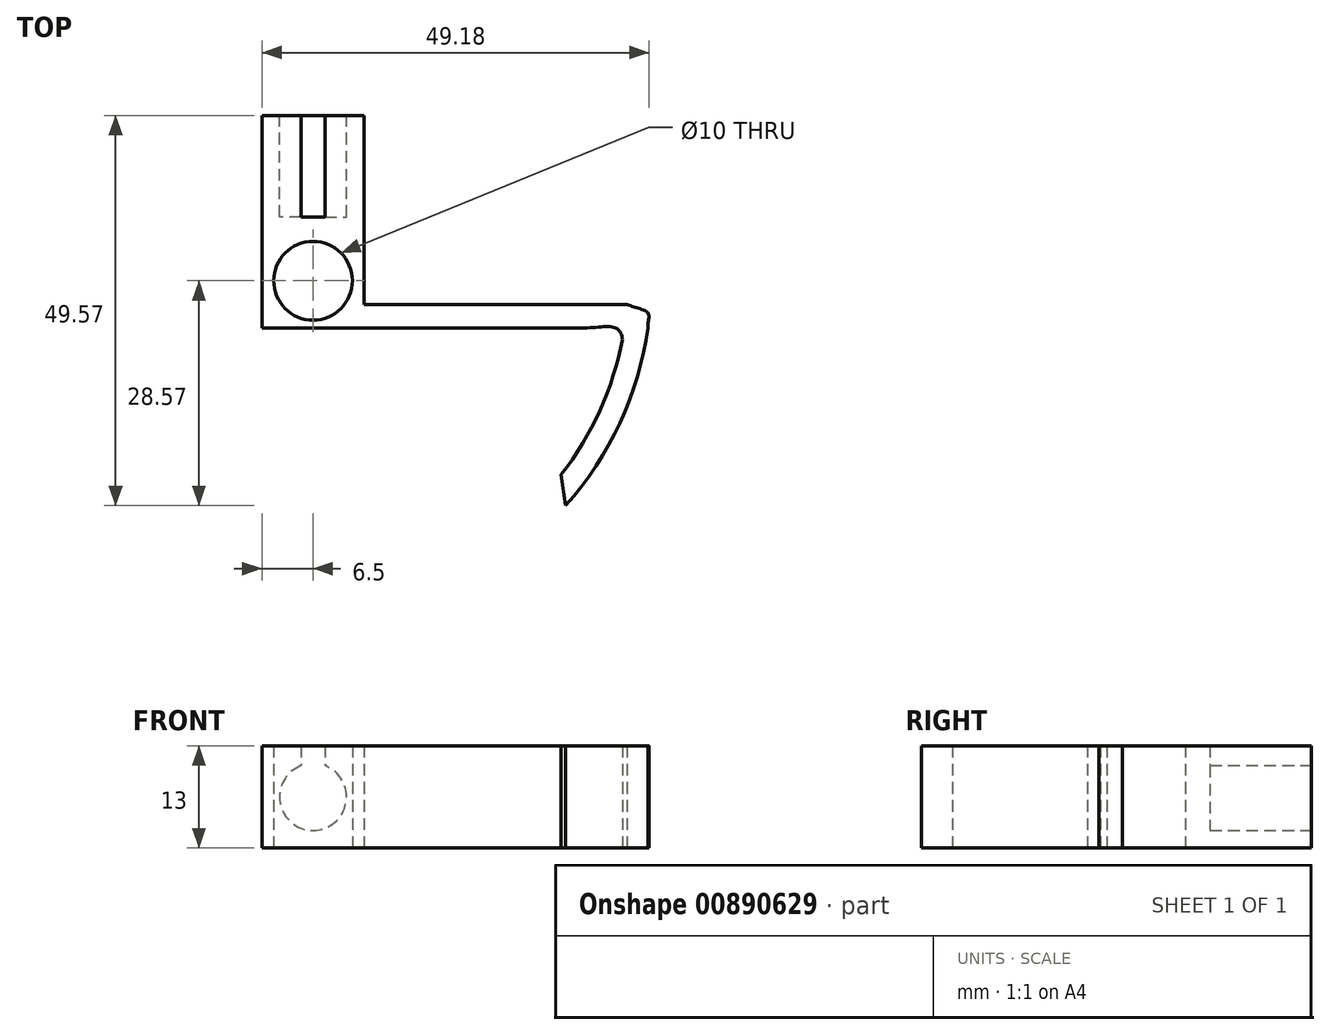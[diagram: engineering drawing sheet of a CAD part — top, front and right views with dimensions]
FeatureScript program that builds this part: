
annotation { "Feature Type Name" : "Feature", "Feature Type Description" : "" }
export const myFeature = defineFeature(function(context is Context, id is Id, definition is map)
    precondition{}
    {
        {
            var Q0;
            Q0=qCreatedBy(makeId("Top.planeOp"),FACE);
            var sketch = newSketch(context, id + "F0", { "sketchPlane" : qUnion([Q0])});
            skCircle(sketch, "E0", {"center": v(0, 0) * mm, "radius": 40 * mm, "construction": true});
            skLineSegment(sketch, "E1", {"start": v(0, 0) * mm, "end": v(-31.52, -24.63) * mm, "construction": true});
            skLineSegment(sketch, "E2", {"start": v(0, 0) * mm, "end": v(31.52, -24.63) * mm, "construction": true});
            skLineSegment(sketch, "E3", {"start": v(-39.89, -3) * mm, "end": v(39.89, -3) * mm, "construction": true});
            skLineSegment(sketch, "E4", {"start": v(-7.53, -3) * mm, "end": v(7, -3) * mm});
            skArc(sketch, "E5", {"start": v(-31.52, -24.63) * mm, "mid": v(-36.73, -15.83) * mm, "end": v(-39.55, -6) * mm});
            skFitSpline(sketch, "E6", {"points": [v(-39.55, -6) * mm, v(-28.95, -3) * mm, v(-24.4, -3) * mm, v(-19.32, -3) * mm, v(-10.02, -3) * mm], "startDerivative": vector(-4.28, 28.2) * mm, "endDerivative": vector(0.87, 0) * mm});
            skLineSegment(sketch, "E7", {"start": v(-39.55, -6) * mm, "end": v(39.55, -6) * mm, "construction": true});
            skLineSegment(sketch, "E8", {"start": v(-31.52, -24.63) * mm, "end": v(31.52, -24.63) * mm, "construction": true});
            skArc(sketch, "E9", {"start": v(-27.52, -24.63) * mm, "mid": v(-33.3, -15.95) * mm, "end": v(-36.44, -6) * mm});
            skArc(sketch, "E10", {"start": v(31.52, -24.63) * mm, "mid": v(36.73, -15.83) * mm, "end": v(39.55, -6) * mm});
            skLineSegment(sketch, "E11", {"start": v(31.52, -24.63) * mm, "end": v(32.1, -28.57) * mm});
            skArc(sketch, "E12", {"start": v(32.1, -28.57) * mm, "mid": v(39, -18.06) * mm, "end": v(42.55, -6) * mm});
            skLineSegment(sketch, "E13", {"start": v(-36.44, -6) * mm, "end": v(33.99, -6) * mm});
            skLineSegment(sketch, "E14", {"start": v(-7.53, -3) * mm, "end": v(-10.02, -3) * mm});
            skLineSegment(sketch, "E15", {"start": v(7, -3) * mm, "end": v(39.89, -3) * mm});
            skLineSegment(sketch, "E16", {"start": v(-31.52, -24.63) * mm, "end": v(-27.52, -24.63) * mm});
            skLineSegment(sketch, "E17", {"start": v(39.55, -6) * mm, "end": v(42.55, -6) * mm, "construction": true});
            skFitSpline(sketch, "E18", {"points": [v(39.89, -3) * mm, v(42.55, -4.09) * mm, v(42.55, -6) * mm], "startDerivative": vector(4.21, -2.12) * mm, "endDerivative": vector(0.52, -5.79) * mm});
            skFitSpline(sketch, "E19", {"points": [v(33.99, -6) * mm, v(38.45, -6) * mm, v(39.3, -7.44) * mm], "startDerivative": vector(9.27, -0.07) * mm, "endDerivative": vector(0.7, -5.18) * mm});
            skLineSegment(sketch, "E20", {"start": v(-6.5, 21) * mm, "end": v(-6.5, -3) * mm});
            skLineSegment(sketch, "E21", {"start": v(-6.5, 21) * mm, "end": v(6.5, 21) * mm});
            skLineSegment(sketch, "E22", {"start": v(6.5, 21) * mm, "end": v(6.5, -3) * mm});
            skLineSegment(sketch, "E23", {"start": v(-6.5, -3) * mm, "end": v(-6.5, -6) * mm});
            skLineSegment(sketch, "E24", {"start": v(7, -3) * mm, "end": v(7, -6) * mm});
            skArc(sketch, "E25", {"start": v(-6.5, -6) * mm, "mid": v(0.25, -8.53) * mm, "end": v(7, -6) * mm});
            skSolve(sketch);
        }
        {
            var Q0;
            Q0=qCreatedBy(makeId("Top.planeOp"),FACE);
            var sketch = newSketch(context, id + "F1", { "sketchPlane" : qUnion([Q0])});
            skCircle(sketch, "E26", {"center": v(0, 0) * mm, "radius": 5 * mm});
            skSolve(sketch);
        }
        {
            var Q0;
            Q0=makeQuery(id+"F0.imprint","IMPRINT",FACE,{"disambiguationData":[TD([[makeQuery(id+"F0.imprint","IMPRINT",EDGE,{"derivedFrom":sQuery(id+"F0.wireOp",EDGE,"E5")}),-1.0]])]});
            var Q1;
            {var subQ0=sQuery(id+"F0.wireOp",EDGE,"E20");Q1=makeQuery(id+"F0.imprint","IMPRINT",FACE,{"disambiguationData":[TD([[makeQuery(id+"F0.imprint","IMPRINT",EDGE,{"derivedFrom":subQ0}),1.0]])]});}
            var Q2;
            {var subQ0=sQuery(id+"F0.wireOp",EDGE,"E11");Q2=makeQuery(id+"F0.imprint","IMPRINT",FACE,{"disambiguationData":[TD([[makeQuery(id+"F0.imprint","IMPRINT",EDGE,{"derivedFrom":subQ0}),1.0]])]});}
            var Q3;
            {var subQ0=sQuery(id+"F0.wireOp",EDGE,"E23");Q3=makeQuery(id+"F0.imprint","IMPRINT",FACE,{"disambiguationData":[TD([[makeQuery(id+"F0.imprint","IMPRINT",EDGE,{"derivedFrom":subQ0}),1.0]])]});}
            extrude(context, id + "F2", {"entities" : qUnion([Q0, Q1, Q2, Q3]), "depth" : 13 * mm, "offsetDistance" : 25 * mm});
        }
        {
            var Q0;
            Q0=makeQuery(id+"F1.imprint","IMPRINT",FACE,{"disambiguationData":[TD([[makeQuery(id+"F1.imprint","IMPRINT",EDGE,{"derivedFrom":sQuery(id+"F1.wireOp",EDGE,"E26")}),1.0]])]});
            var Q1;
            Q1=makeQuery(id+"F2.opExtrude","CAP_FACE",FACE,{"disambiguationData":[OSD([sQuery(id+"F0.wireOp",EDGE,"E4"),sQuery(id+"F0.wireOp",EDGE,"E5"),sQuery(id+"F0.wireOp",EDGE,"E6"),sQuery(id+"F0.wireOp",EDGE,"E9"),sQuery(id+"F0.wireOp",EDGE,"E10"),sQuery(id+"F0.wireOp",EDGE,"E11"),sQuery(id+"F0.wireOp",EDGE,"E12"),sQuery(id+"F0.wireOp",EDGE,"E13"),sQuery(id+"F0.wireOp",EDGE,"E14"),sQuery(id+"F0.wireOp",EDGE,"E15"),sQuery(id+"F0.wireOp",EDGE,"E16"),sQuery(id+"F0.wireOp",EDGE,"E18"),sQuery(id+"F0.wireOp",EDGE,"E19"),sQuery(id+"F0.wireOp",EDGE,"E20"),sQuery(id+"F0.wireOp",EDGE,"E21"),sQuery(id+"F0.wireOp",EDGE,"E22"),sQuery(id+"F0.wireOp",EDGE,"E25")])],"isStart":false});
            extrude(context, id + "F3", {"entities" : qUnion([Q0]), "operationType" : NewBodyOperationType.REMOVE, "endBound" : BoundingType.UP_TO_SURFACE, "depth" : 25 * mm, "endBoundEntityFace" : qUnion([Q1]), "offsetDistance" : 25 * mm});
        }
        {
            var Q0;
            Q0=makeQuery(id+"F2.opExtrude","SWEPT_FACE",FACE,{"disambiguationData":[OSD([sQuery(id+"F0.wireOp",EDGE,"E21")])]});
            var sketch = newSketch(context, id + "F4", { "sketchPlane" : qUnion([Q0])});
            skLineSegment(sketch, "E27", {"start": v(-6.5, 6.5) * mm, "end": v(0, 6.5) * mm, "construction": true});
            skCircle(sketch, "E28", {"center": v(0, 6.5) * mm, "radius": 4.25 * mm});
            skLineSegment(sketch, "E29", {"start": v(-1.5, 13) * mm, "end": v(-1.5, 10.48) * mm});
            skLineSegment(sketch, "E30", {"start": v(1.5, 13) * mm, "end": v(1.5, 10.48) * mm});
            skSolve(sketch);
        }
        {
            var Q0;
            {var subQ0=sQuery(id+"F4.wireOp",EDGE,"E28");var subQ1=makeQuery(id+"F4.imprint","INTERSECT",VERTEX,{"derivedFrom":[subQ0,sQuery(id+"F4.wireOp",EDGE,"E29")]});Q0=makeQuery(id+"F4.imprint","IMPRINT",FACE,{"disambiguationData":[TD([[makeQuery(id+"F4.imprint","IMPRINT",EDGE,{"disambiguationData":[TD([[subQ1,1.0]])],"derivedFrom":subQ0}),1.0]])]});}
            var Q1;
            {var subQ0=sQuery(id+"F4.wireOp",EDGE,"E29");Q1=makeQuery(id+"F4.imprint","IMPRINT",FACE,{"disambiguationData":[TD([[makeQuery(id+"F4.imprint","IMPRINT",EDGE,{"derivedFrom":subQ0}),1.0]])]});}
            extrude(context, id + "F5", {"entities" : qUnion([Q0, Q1]), "operationType" : NewBodyOperationType.REMOVE, "oppositeDirection" : true, "depth" : 12.9 * mm, "offsetDistance" : 25 * mm});
        }
    });
